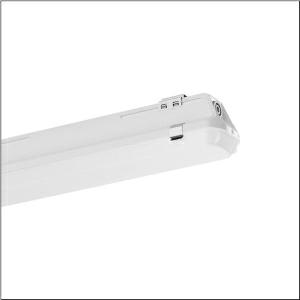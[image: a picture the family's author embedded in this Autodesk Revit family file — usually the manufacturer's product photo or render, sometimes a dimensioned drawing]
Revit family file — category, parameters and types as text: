
# Revit family: monsun_r__21_parking_51fg20dp440bhd_61d3
name_source: partatom
category: Lighting Fixtures
units: mm (PartAtom-declared; Revit-internal decimal feet)

## family parameters
Cut with Voids When Loaded = No
Host = Face
Light Source = No
Part Type = Normal
Room Calculation Point = No
Round Connector Dimension = Use Diameter
Shared = No

## types (1)
- --- (1 x LED, 4810 lm, 37.4 W, 4000K)
    Apparent Load = 37 VA
    CIE Flux Codes = 45 75 93 94 100
    Color Rendering = 80
    Color Temperature = 4000K
    Default Elevation = 1800 mm
    Description = Monsun® 21 parking, damp-proof luminaire, chain hanger, primary optical cover: enclosure, of PC, light emission: direct distribution, primary light characteristic: symmetric, installation type: suspended mounting, surface-mounted, horizontal mounting, vertical mounting, LED, rated luminous flux: 4.810lm, luminous efficacy: 129lm/W, light colour: 840, colour temperature: 4000K, control gear: ECG DALI, with terminal, 5-pole, max. 2.5mm², mains connection: 220..240V, AC, 50/60Hz, rated input power: 37W, housing, of glass-fibre reinforced polyester, uncoated, bright grey, incl. chain hanger, length: 1.590mm, width: 90mm, height: 88mm, clip for enclosure, of stainless steel (V2A), ceiling mounting element, of stainless steel (V2A), chain hanger, of stainless steel (V2A), DALIeco controller, master, sensor HC1, protection rating (complete): IP66, insulation class (complete): insulation class I (protective earthing), certification: CE, ENEC, VDE, UKCA, protection symbol: D, impact resistance: IK08, permissible operating ambient temperature: -20..+35°C, standard: EN 50419, EN 60598-2-1, corresponds to IFS (International Featured Standards) requirements for safety and quality in the food industry, for indoor or canopied outdoor use, no direct snow, no direct sun, no direct rain, contact your sales advisor before using the luminaires in applications with unclear chemical exposure, large temperature fluctuations or condensation-forming humidity, LABS conformity tested according to VDMA 24364:2018-05, packaging unit: 1 piece
    Height = 89 mm
    Lamp = 1 x LED
    Lamp Light Flux = 4810 lm
    Lamp Power = 37.4 W
    Lamp count = 1
    Length = 1590 mm
    Luminous efficacy = 129 lm/W
    Manufacturer = Siteco
    ModVariant = No
    Model = 51FG20DP440BHD
    Mounting Place = Ceiling
    Mounting Type = Surface mounted
    Number of Poles = 1
    OnlyDefault = Yes
    Power Factor = 1
    Product Name = Monsun® 21 parking
    Product group = damp-proof luminaire
    ProductGroupID = 300
    Protection Class = Protection class I
    Protection Degree = IP 66
    RLX_Detail_Level = 1
    RLX_Emergency_Light_Flux = 0 lm
    RLX_Emergency_Type = 0
    RLX_Emergency_Type_DB = No
    RlxData = <blob elided: 92429 chars, md5=25157a00>
    Socket = socket
    Standby Power = 0 W
    System Light Flux = 4810 lm
    System Power = 37 W
    Type Comments = factory setting: luminous flux: 100 % | dim-lin: 254 | 228 mA
    Type Image = l_1006717.jpg
    URL = http://relux.com
    VarID = @adj_133999
    Voltage = 0 V
    Weight = 0.00 kg
    Width = 90 mm

## geometry (parser evidence)
native form markers: Blend x4, Sweep x13
no freeform markers — native parametric forms only
